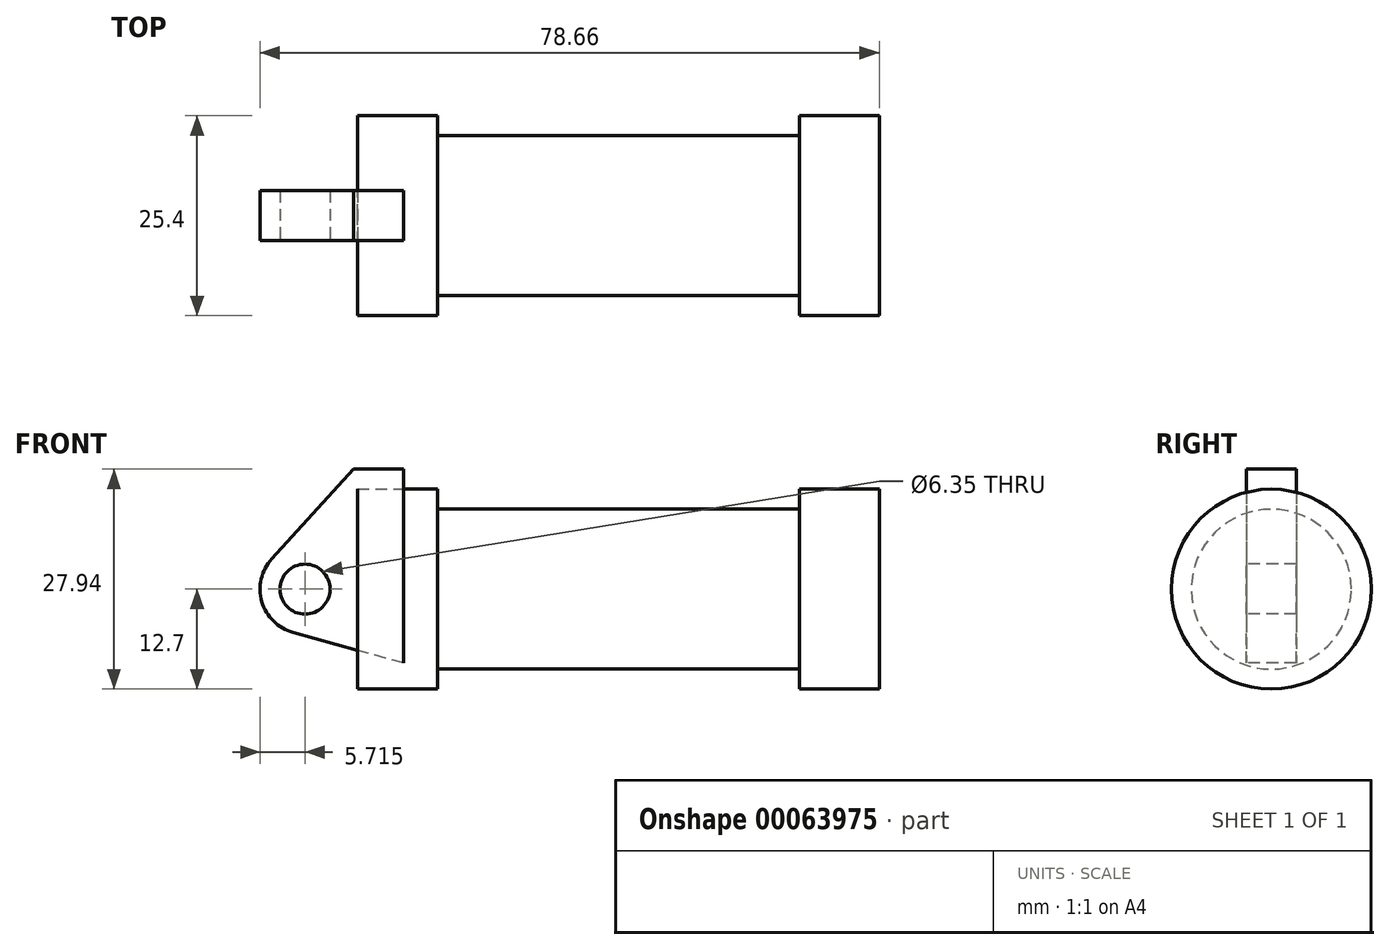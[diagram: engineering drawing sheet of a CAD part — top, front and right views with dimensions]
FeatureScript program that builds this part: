
annotation { "Feature Type Name" : "Feature", "Feature Type Description" : "" }
export const myFeature = defineFeature(function(context is Context, id is Id, definition is map)
    precondition{}
    {
        {
            var Q0;
            Q0=qCreatedBy(makeId("Front.planeOp"),FACE);
            var sketch = newSketch(context, id + "F0", { "sketchPlane" : qUnion([Q0])});
            skLineSegment(sketch, "E0", {"start": v(0, 0) * mm, "end": v(0, 12.7) * mm});
            skLineSegment(sketch, "E1", {"start": v(0, 12.7) * mm, "end": v(10.16, 12.7) * mm});
            skLineSegment(sketch, "E2", {"start": v(10.16, 12.7) * mm, "end": v(10.16, 10.16) * mm});
            skLineSegment(sketch, "E3", {"start": v(10.16, 10.16) * mm, "end": v(56.13, 10.16) * mm});
            skLineSegment(sketch, "E4", {"start": v(56.13, 10.16) * mm, "end": v(56.13, 12.7) * mm});
            skLineSegment(sketch, "E5", {"start": v(56.13, 12.7) * mm, "end": v(66.3, 12.7) * mm});
            skLineSegment(sketch, "E6", {"start": v(66.3, 12.7) * mm, "end": v(66.3, 0) * mm});
            skLineSegment(sketch, "E7", {"start": v(66.3, 0) * mm, "end": v(0, 0) * mm});
            skLineSegment(sketch, "E8", {"start": v(5.84, 15.24) * mm, "end": v(-0.5, 15.24) * mm});
            skLineSegment(sketch, "E9", {"start": v(-0.5, 15.24) * mm, "end": v(-10.88, 3.85) * mm});
            skLineSegment(sketch, "E10", {"start": v(0, 0) * mm, "end": v(-6.65, 0) * mm});
            skCircle(sketch, "E11", {"center": v(-6.65, 0) * mm, "radius": 5.72 * mm});
            skCircle(sketch, "E12", {"center": v(-6.65, 0) * mm, "radius": 3.18 * mm});
            skLineSegment(sketch, "E13", {"start": v(5.84, 15.24) * mm, "end": v(5.84, -9.4) * mm});
            skLineSegment(sketch, "E14", {"start": v(5.84, -9.4) * mm, "end": v(-8.18, -5.5) * mm});
            skSolve(sketch);
        }
        {
            var Q0;
            {var subQ0=sQuery(id+"F0.wireOp",EDGE,"E0");Q0=makeQuery(id+"F0.imprint","IMPRINT",FACE,{"disambiguationData":[TD([[makeQuery(id+"F0.imprint","IMPRINT",EDGE,{"derivedFrom":subQ0}),-1.0]])]});}
            var Q1;
            {var subQ3=sQuery(id+"F0.wireOp",EDGE,"E0");Q1=makeQuery(id+"F0.imprint","IMPRINT",FACE,{"disambiguationData":[TD([[makeQuery(id+"F0.imprint","IMPRINT",EDGE,{"derivedFrom":subQ3}),1.0]])]});}
            var Q2;
            {var subQ0=sQuery(id+"F0.wireOp",EDGE,"E14");Q2=makeQuery(id+"F0.imprint","IMPRINT",FACE,{"disambiguationData":[TD([[makeQuery(id+"F0.imprint","IMPRINT",EDGE,{"derivedFrom":subQ0}),-1.0]])]});}
            var Q3;
            {var subQ4=sQuery(id+"F0.wireOp",EDGE,"E12");Q3=makeQuery(id+"F0.imprint","IMPRINT",FACE,{"disambiguationData":[TD([[makeQuery(id+"F0.imprint","IMPRINT",EDGE,{"derivedFrom":subQ4}),-1.0]])]});}
            extrude(context, id + "F1", {"entities" : qUnion([Q0, Q1, Q2, Q3]), "oppositeDirection" : true, "depth" : 3.17 * mm});
        }
        {
            var Q0;
            {var subQ0=sQuery(id+"F0.wireOp",EDGE,"E14");Q0=makeQuery(id+"F0.imprint","IMPRINT",FACE,{"disambiguationData":[TD([[makeQuery(id+"F0.imprint","IMPRINT",EDGE,{"derivedFrom":subQ0}),-1.0]])]});}
            var Q1;
            {var subQ0=sQuery(id+"F0.wireOp",EDGE,"E0");Q1=makeQuery(id+"F0.imprint","IMPRINT",FACE,{"disambiguationData":[TD([[makeQuery(id+"F0.imprint","IMPRINT",EDGE,{"derivedFrom":subQ0}),-1.0]])]});}
            var Q2;
            {var subQ3=sQuery(id+"F0.wireOp",EDGE,"E0");Q2=makeQuery(id+"F0.imprint","IMPRINT",FACE,{"disambiguationData":[TD([[makeQuery(id+"F0.imprint","IMPRINT",EDGE,{"derivedFrom":subQ3}),1.0]])]});}
            var Q3;
            {var subQ4=sQuery(id+"F0.wireOp",EDGE,"E12");Q3=makeQuery(id+"F0.imprint","IMPRINT",FACE,{"disambiguationData":[TD([[makeQuery(id+"F0.imprint","IMPRINT",EDGE,{"derivedFrom":subQ4}),-1.0]])]});}
            extrude(context, id + "F2", {"entities" : qUnion([Q0, Q1, Q2, Q3]), "operationType" : NewBodyOperationType.ADD, "depth" : 3.17 * mm});
        }
        {
            var Q0;
            {var subQ0=sQuery(id+"F0.wireOp",EDGE,"E0");Q0=makeQuery(id+"F0.imprint","IMPRINT",FACE,{"disambiguationData":[TD([[makeQuery(id+"F0.imprint","IMPRINT",EDGE,{"derivedFrom":subQ0}),-1.0]])]});}
            var Q1;
            {var subQ0=sQuery(id+"F0.wireOp",EDGE,"E2");Q1=makeQuery(id+"F0.imprint","IMPRINT",FACE,{"disambiguationData":[TD([[makeQuery(id+"F0.imprint","IMPRINT",EDGE,{"derivedFrom":subQ0}),-1.0]])]});}
            var Q2;
            Q2=sQuery(id+"F0.wireOp",EDGE,"E7");
            revolve(context, id + "F3", {"entities" : qUnion([Q0, Q1]), "axis" : qUnion([Q2]), "revolveType" : RevolveType.FULL});
        }
        {
            var Q0;
            Q0=makeQuery(id+"F3.opRevolve","SWEPT_FACE",FACE,{"disambiguationData":[OSD([sQuery(id+"F0.wireOp",EDGE,"E6")])]});
            var sketch = newSketch(context, id + "F4", { "sketchPlane" : qUnion([Q0])});
            skCircle(sketch, "E15", {"center": v(0, 0) * mm, "radius": 5.08 * mm});
            skCircle(sketch, "E16", {"center": v(0, 0) * mm, "radius": 1.52 * mm});
            skLineSegment(sketch, "E17", {"start": v(-5.08, 15.24) * mm, "end": v(-5.08, 0) * mm});
            skLineSegment(sketch, "E18", {"start": v(-5.08, 15.24) * mm, "end": v(5.08, 15.24) * mm});
            skLineSegment(sketch, "E19", {"start": v(5.08, 15.24) * mm, "end": v(5.08, 0) * mm});
            skSolve(sketch);
        }
        {
            var Q0;
            Q0=sQuery(id+"F4.wireOp",EDGE,"E16");
            extrude(context, id + "F5", {"bodyType" : ToolBodyType.SURFACE, "surfaceEntities" : qUnion([Q0]), "depth" : 25.4 * mm});
        }
    });
